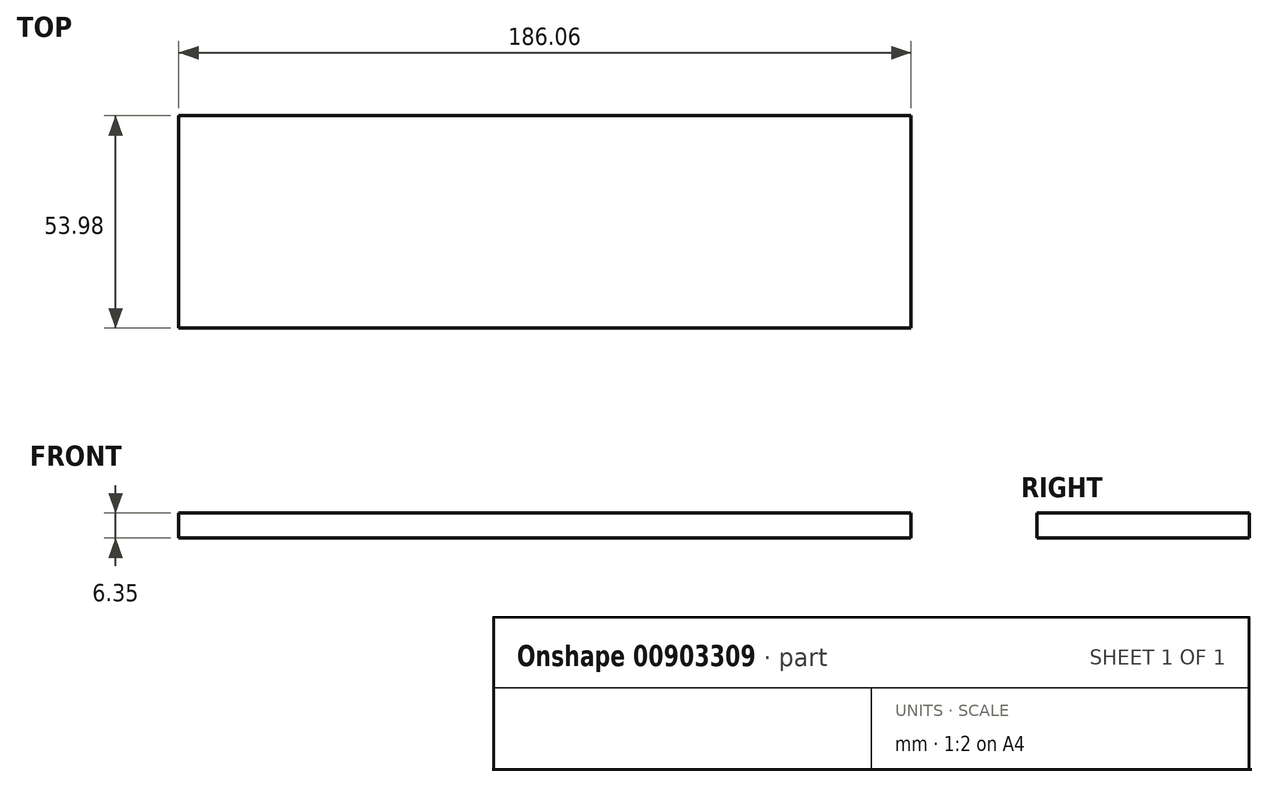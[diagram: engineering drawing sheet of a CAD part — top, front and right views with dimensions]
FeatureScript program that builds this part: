
annotation { "Feature Type Name" : "Feature", "Feature Type Description" : "" }
export const myFeature = defineFeature(function(context is Context, id is Id, definition is map)
    precondition{}
    {
        {
            var Q0;
            Q0=qCreatedBy(makeId("Top.planeOp"),FACE);
            var sketch = newSketch(context, id + "F0", { "sketchPlane" : qUnion([Q0])});
            skLineSegment(sketch, "E0.bottom", {"start": v(0, 0) * mm, "end": v(186.06, 0) * mm});
            skLineSegment(sketch, "E0.top", {"start": v(0, -53.97) * mm, "end": v(186.06, -53.97) * mm});
            skLineSegment(sketch, "E0.left", {"start": v(0, 0) * mm, "end": v(0, -53.97) * mm});
            skLineSegment(sketch, "E0.right", {"start": v(186.06, 0) * mm, "end": v(186.06, -53.97) * mm});
            skSolve(sketch);
        }
        {
            var Q0;
            Q0=makeQuery(id+"F0.imprint","IMPRINT",FACE,{"disambiguationData":[TD([[makeQuery(id+"F0.imprint","IMPRINT",EDGE,{"derivedFrom":sQuery(id+"F0.wireOp",EDGE,"E0.bottom")}),-1.0]])]});
            extrude(context, id + "F1", {"entities" : qUnion([Q0]), "depth" : 6.35 * mm, "offsetDistance" : 25.4 * mm});
        }
    });
